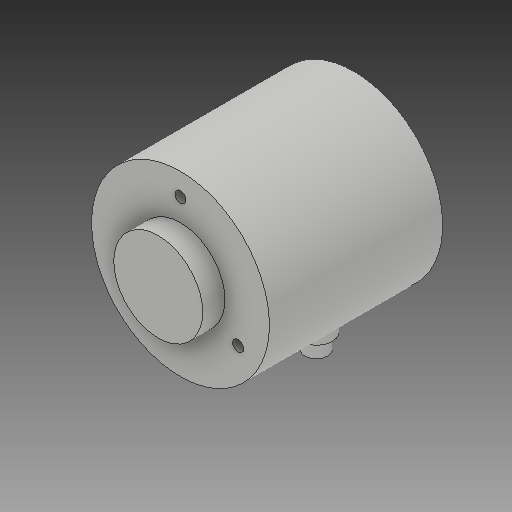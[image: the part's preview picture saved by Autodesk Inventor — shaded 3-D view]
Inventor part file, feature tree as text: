
AUTODESK INVENTOR PART (.ipt)
format: ipt  version: 2018 (Build 220112000, 112)  size: 154,624 bytes
history: native  units: mm
features: sketch x5, extrude x4, hole x1, plane x1, projected_geometry x1
ambient origin geometry x8: Origin, YZ Plane, XZ Plane, XY Plane, X Axis, Y Axis, Z Axis, Center Point
bodies: Solid1 (feature_tree)
feature tree (12):
  extrude  "Extrusion1"  Depth=39.0mm TaperAngle=0.0deg
  extrude  "Extrusion2"  Depth=20.0mm TaperAngle=0.0deg
  hole  "Hole1"  [1 undecoded]
  plane  "Work Plane2"
  extrude  "Extrusion6"  Depth=7.3mm
  extrude  "Extrusion7"  Depth=10.0mm
  sketch  "Sketch1"  dims[d0=40.0mm d1=39.0mm d2=0.0mm]
  sketch  "Sketch2"  dims[d3=20.0mm d4=5.0mm d5=0.0mm]
  sketch  "Sketch3"  dims[d6=30.0mm d7=30.0mm d9=360.0deg]
  sketch  "Sketch6"  dims[d11=2.459mm d12=7.0mm d13=4.0mm d14=2.0mm d15=90.0deg d16=9.8mm d17=20.594885mm d25=7.3mm]
  projected_geometry  "Projected Loop2"
  sketch  "Sketch7"  dims[d26=8.47mm d29=0.9mm d30=6.58mm d31=0.0mm d32=5.1mm d33=10.0mm d34=0.0mm d35=3.29mm d36=0.0mm]
note: 1 required parameter value undecoded (feature->parameter linkage not recoverable at this tier; creation-order binding heuristic only, values carry confidence <= 0.55)
